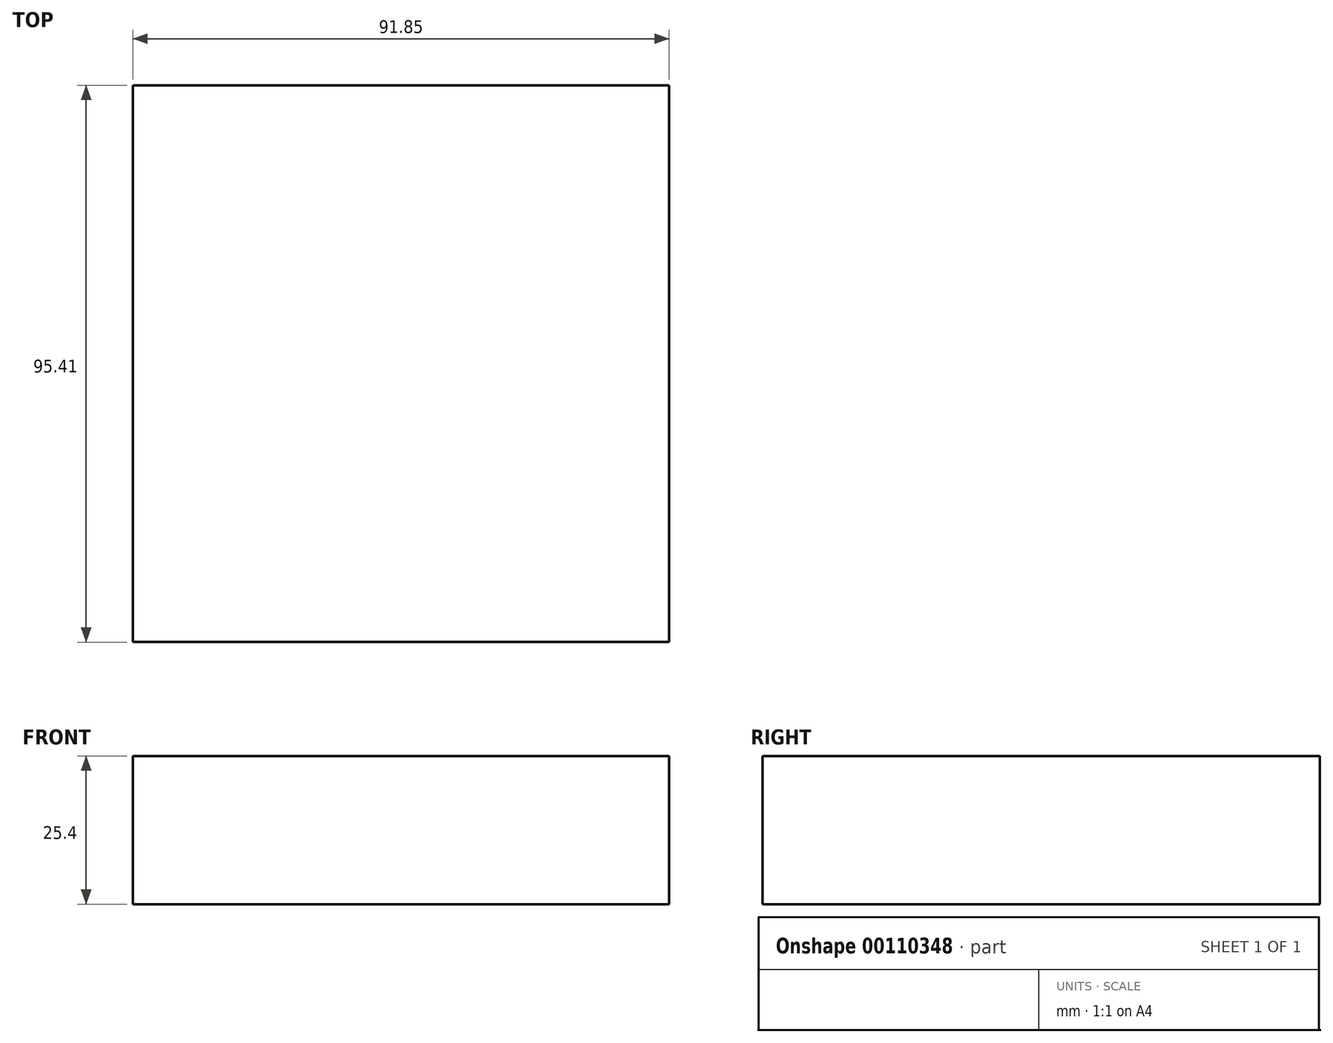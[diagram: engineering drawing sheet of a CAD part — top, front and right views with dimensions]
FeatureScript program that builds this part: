
annotation { "Feature Type Name" : "Feature", "Feature Type Description" : "" }
export const myFeature = defineFeature(function(context is Context, id is Id, definition is map)
    precondition{}
    {
        {
            var Q0;
            Q0=qCreatedBy(makeId("Top.planeOp"),FACE);
            var sketch = newSketch(context, id + "F0", { "sketchPlane" : qUnion([Q0])});
            skLineSegment(sketch, "E0.bottom", {"start": v(-53.88, -49.87) * mm, "end": v(37.97, -49.87) * mm});
            skLineSegment(sketch, "E0.top", {"start": v(-53.88, 45.54) * mm, "end": v(37.97, 45.54) * mm});
            skLineSegment(sketch, "E0.left", {"start": v(-53.88, -49.87) * mm, "end": v(-53.88, 45.54) * mm});
            skLineSegment(sketch, "E0.right", {"start": v(37.97, -49.87) * mm, "end": v(37.97, 45.54) * mm});
            skSolve(sketch);
        }
        {
            var Q0;
            Q0=makeQuery(id+"F0.imprint","IMPRINT",FACE,{"disambiguationData":[TD([[makeQuery(id+"F0.imprint","IMPRINT",EDGE,{"derivedFrom":sQuery(id+"F0.wireOp",EDGE,"E0.bottom")}),1.0]])]});
            extrude(context, id + "F1", {"entities" : qUnion([Q0]), "depth" : 25.4 * mm});
        }
    });
